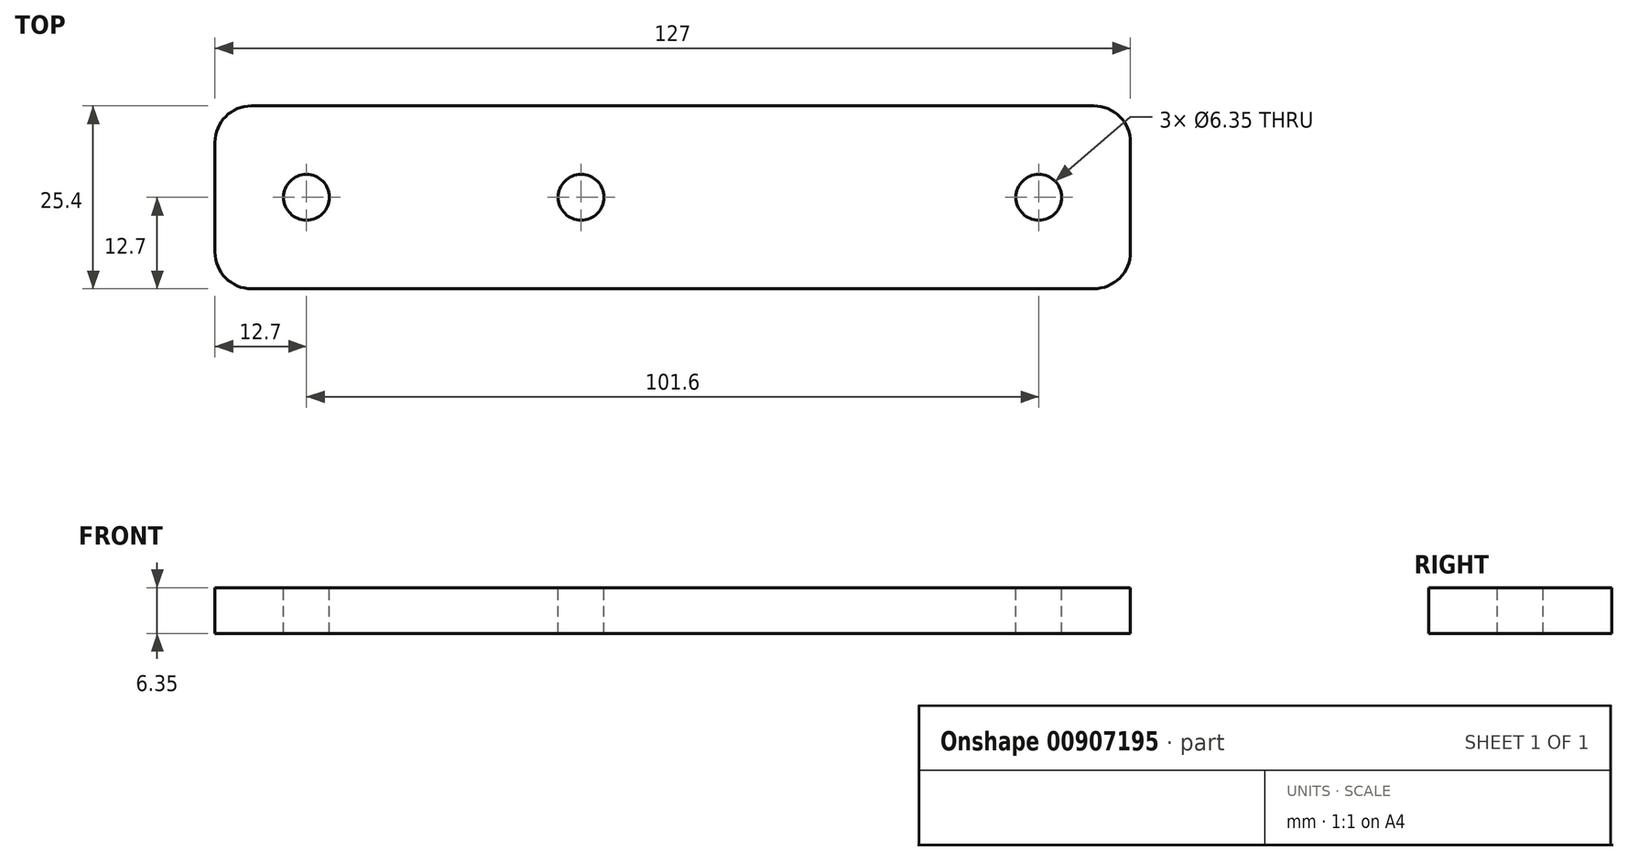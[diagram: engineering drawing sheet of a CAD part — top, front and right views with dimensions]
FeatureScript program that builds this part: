
annotation { "Feature Type Name" : "Feature", "Feature Type Description" : "" }
export const myFeature = defineFeature(function(context is Context, id is Id, definition is map)
    precondition{}
    {
        {
            var Q0;
            Q0=qCreatedBy(makeId("Top.planeOp"),FACE);
            var sketch = newSketch(context, id + "F0", { "sketchPlane" : qUnion([Q0])});
            skLineSegment(sketch, "E0.bottom", {"start": v(5.08, 0) * mm, "end": v(121.92, 0) * mm});
            skLineSegment(sketch, "E0.top", {"start": v(5.08, 25.4) * mm, "end": v(121.92, 25.4) * mm});
            skLineSegment(sketch, "E0.left", {"start": v(0, 5.08) * mm, "end": v(0, 20.32) * mm});
            skLineSegment(sketch, "E0.right", {"start": v(127, 5.08) * mm, "end": v(127, 20.32) * mm});
            skCircle(sketch, "E1", {"center": v(114.3, 12.7) * mm, "radius": 3.18 * mm});
            skCircle(sketch, "E2", {"center": v(12.7, 12.7) * mm, "radius": 3.18 * mm});
            skPoint(sketch, "E3.visualSharp", {"position": v(0, 25.4) * mm});
            skArc(sketch, "E3.filletArc", {"start": v(5.08, 25.4) * mm, "mid": v(1.49, 23.91) * mm, "end": v(0, 20.32) * mm});
            skPoint(sketch, "E4.visualSharp", {"position": v(0, 0) * mm});
            skArc(sketch, "E4.filletArc", {"start": v(0, 5.08) * mm, "mid": v(1.49, 1.49) * mm, "end": v(5.08, 0) * mm});
            skPoint(sketch, "E5.visualSharp", {"position": v(127, 0) * mm});
            skArc(sketch, "E5.filletArc", {"start": v(121.92, 0) * mm, "mid": v(125.51, 1.49) * mm, "end": v(127, 5.08) * mm});
            skPoint(sketch, "E6.visualSharp", {"position": v(127, 25.4) * mm});
            skArc(sketch, "E6.filletArc", {"start": v(127, 20.32) * mm, "mid": v(125.51, 23.91) * mm, "end": v(121.92, 25.4) * mm});
            skCircle(sketch, "E7", {"center": v(50.8, 12.7) * mm, "radius": 3.18 * mm});
            skSolve(sketch);
        }
        {
            var Q0;
            Q0=makeQuery(id+"F0.imprint","IMPRINT",FACE,{"disambiguationData":[TD([[makeQuery(id+"F0.imprint","IMPRINT",EDGE,{"derivedFrom":sQuery(id+"F0.wireOp",EDGE,"E0.bottom")}),1.0]])]});
            extrude(context, id + "F1", {"entities" : qUnion([Q0]), "oppositeDirection" : true, "depth" : 6.35 * mm, "offsetDistance" : 25.4 * mm});
        }
    });
